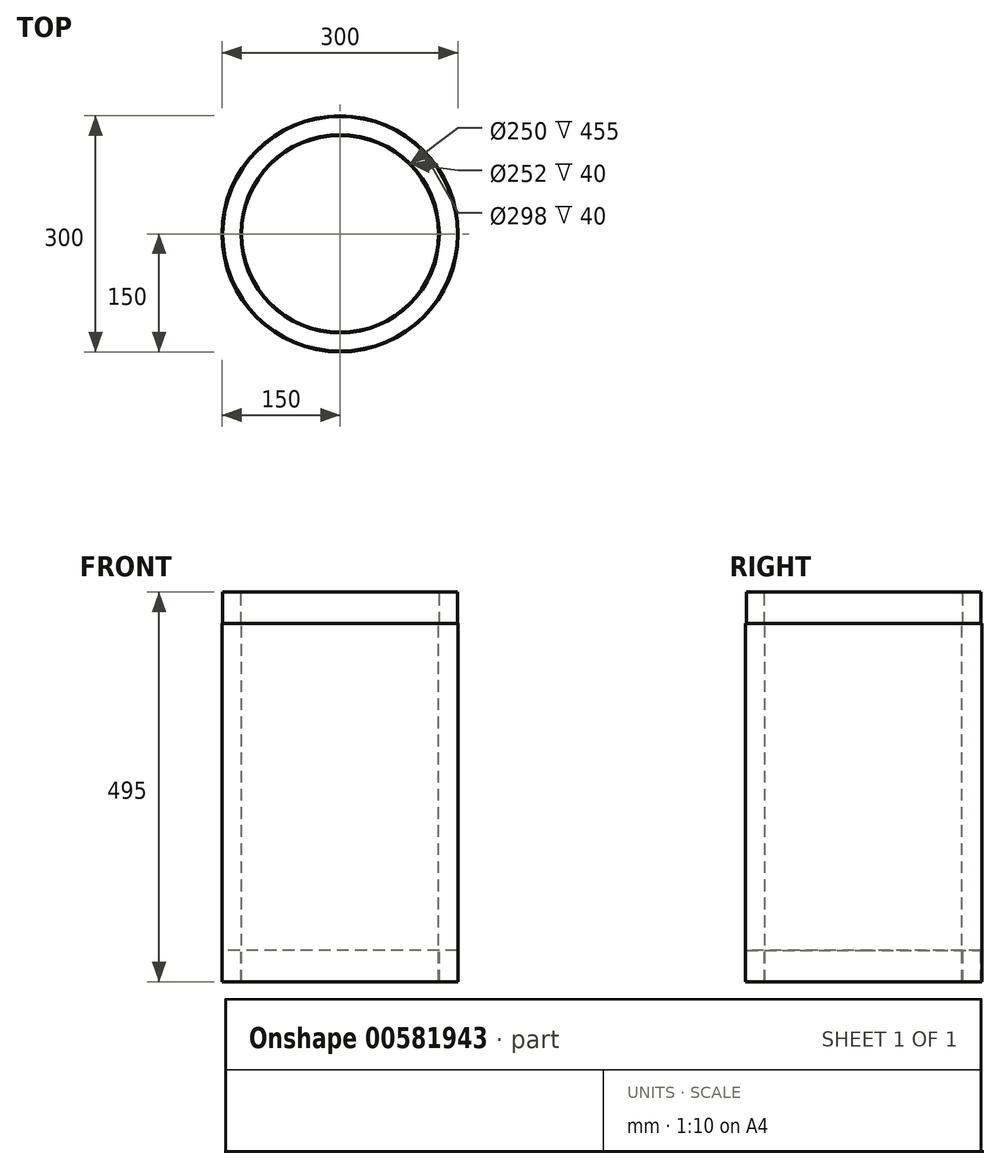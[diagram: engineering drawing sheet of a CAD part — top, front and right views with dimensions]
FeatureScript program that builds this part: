
annotation { "Feature Type Name" : "Feature", "Feature Type Description" : "" }
export const myFeature = defineFeature(function(context is Context, id is Id, definition is map)
    precondition{}
    {
        {
            var Q0;
            Q0=qCreatedBy(makeId("Front.planeOp"),FACE);
            var sketch = newSketch(context, id + "F0", { "sketchPlane" : qUnion([Q0])});
            skLineSegment(sketch, "E0", {"start": v(0, 345.75) * mm, "end": v(0, -558.03) * mm, "construction": true});
            skLineSegment(sketch, "E1", {"start": v(-125, -518.84) * mm, "end": v(-125, -63.84) * mm});
            skLineSegment(sketch, "E2", {"start": v(-125, -63.84) * mm, "end": v(-126, -63.84) * mm});
            skLineSegment(sketch, "E3", {"start": v(-126, -63.84) * mm, "end": v(-126, -23.84) * mm});
            skLineSegment(sketch, "E4", {"start": v(-126, -23.84) * mm, "end": v(-149, -23.84) * mm});
            skLineSegment(sketch, "E5", {"start": v(-149, -23.84) * mm, "end": v(-149, -63.84) * mm});
            skLineSegment(sketch, "E6", {"start": v(-149, -63.84) * mm, "end": v(-150, -63.84) * mm});
            skLineSegment(sketch, "E7", {"start": v(-150, -63.84) * mm, "end": v(-150, -518.84) * mm});
            skLineSegment(sketch, "E8", {"start": v(-150, -518.84) * mm, "end": v(-149, -518.84) * mm});
            skLineSegment(sketch, "E9", {"start": v(-149, -518.84) * mm, "end": v(-149, -478.84) * mm});
            skLineSegment(sketch, "E10", {"start": v(-149, -478.84) * mm, "end": v(-126, -478.84) * mm});
            skLineSegment(sketch, "E11", {"start": v(-126, -478.84) * mm, "end": v(-126, -518.84) * mm});
            skLineSegment(sketch, "E12", {"start": v(-126, -518.84) * mm, "end": v(-125, -518.84) * mm});
            skSolve(sketch);
        }
        {
            var Q0;
            Q0=qSketchRegion(id+"F0",true);
            var Q1;
            Q1=sQuery(id+"F0.wireOp",EDGE,"E0");
            revolve(context, id + "F1", {"entities" : qUnion([Q0]), "axis" : qUnion([Q1]), "revolveType" : RevolveType.FULL});
        }
    });
